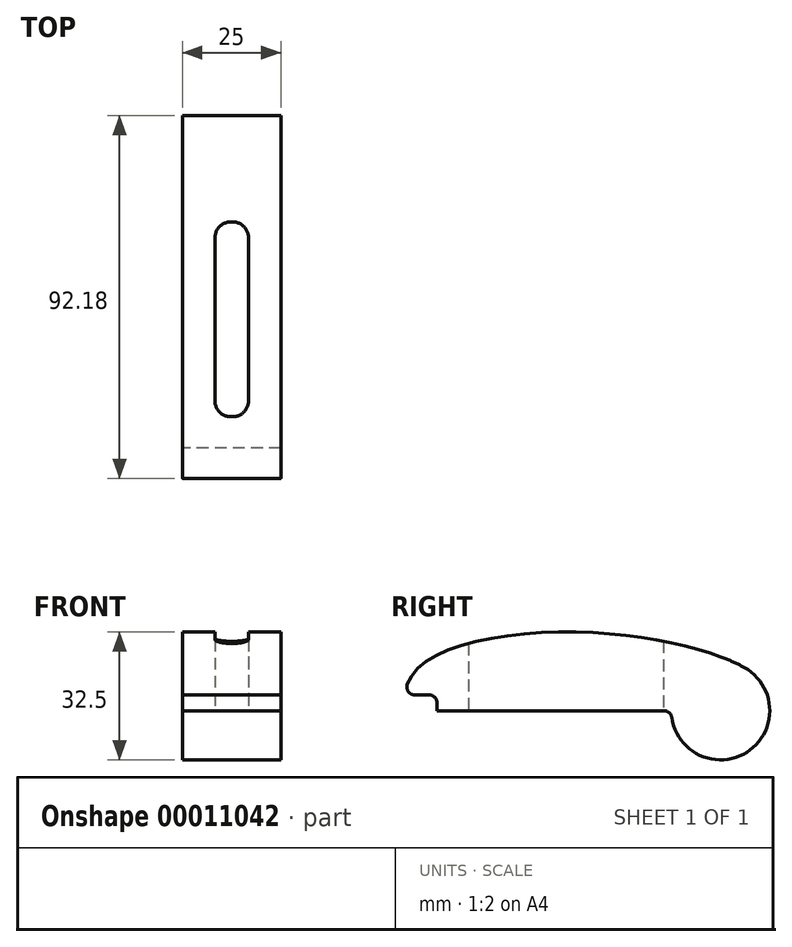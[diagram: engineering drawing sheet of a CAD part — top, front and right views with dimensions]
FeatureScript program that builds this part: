
annotation { "Feature Type Name" : "Feature", "Feature Type Description" : "" }
export const myFeature = defineFeature(function(context is Context, id is Id, definition is map)
    precondition{}
    {
        {
            var Q0;
            Q0=qCreatedBy(makeId("Right.planeOp"),FACE);
            var sketch = newSketch(context, id + "F0", { "sketchPlane" : qUnion([Q0])});
            skCircle(sketch, "E0", {"center": v(80, 0) * mm, "radius": 12.5 * mm});
            skLineSegment(sketch, "E1.bottom", {"start": v(0, 0) * mm, "end": v(80, 0) * mm});
            skLineSegment(sketch, "E1.top", {"start": v(0, 15) * mm, "end": v(80, 15) * mm, "construction": true});
            skLineSegment(sketch, "E1.left", {"start": v(0, 0) * mm, "end": v(0, 15) * mm, "construction": true});
            skLineSegment(sketch, "E1.right", {"start": v(80, 0) * mm, "end": v(80, 15) * mm});
            skLineSegment(sketch, "E2.bottom", {"start": v(0, 0) * mm, "end": v(8, 0) * mm});
            skLineSegment(sketch, "E2.top", {"start": v(0, 4) * mm, "end": v(8, 4) * mm});
            skLineSegment(sketch, "E2.left", {"start": v(0, 0) * mm, "end": v(0, 4) * mm});
            skLineSegment(sketch, "E2.right", {"start": v(8, 0) * mm, "end": v(8, 4) * mm});
            skFitSpline(sketch, "E3", {"points": [v(0, 4) * mm, v(40, 20) * mm, v(86.9, 10.42) * mm], "startDerivative": vector(0, 67.79) * mm, "endDerivative": vector(40.4, -26.8) * mm});
            skSolve(sketch);
        }
        {
            var Q0;
            {var subQ1=sQuery(id+"F0.wireOp",EDGE,"E0");var subQ6=makeQuery(id+"F0.imprint","INTERSECT",VERTEX,{"derivedFrom":[subQ1,sQuery(id+"F0.wireOp",EDGE,"E3")]});Q0=makeQuery(id+"F0.imprint","IMPRINT",FACE,{"disambiguationData":[TD([[makeQuery(id+"F0.imprint","IMPRINT",EDGE,{"disambiguationData":[TD([[subQ6,-1.0]])],"derivedFrom":subQ1}),1.0]])]});}
            var Q1;
            {var subQ0=sQuery(id+"F0.wireOp",EDGE,"E3");var subQ3=sQuery(id+"F0.wireOp",EDGE,"E0");var subQ4=makeQuery(id+"F0.imprint","INTERSECT",VERTEX,{"derivedFrom":[subQ3,subQ0]});Q1=makeQuery(id+"F0.imprint","IMPRINT",FACE,{"disambiguationData":[TD([[makeQuery(id+"F0.imprint","IMPRINT",EDGE,{"disambiguationData":[TD([[subQ4,-1.0]])],"derivedFrom":subQ3}),-1.0]])]});}
            var Q2;
            {var subQ1=sQuery(id+"F0.wireOp",EDGE,"E0");var subQ3=sQuery(id+"F0.wireOp",EDGE,"E1.bottom");var subQ5=makeQuery(id+"F0.imprint","INTERSECT",VERTEX,{"derivedFrom":[subQ1,subQ3]});Q2=makeQuery(id+"F0.imprint","IMPRINT",FACE,{"disambiguationData":[TD([[makeQuery(id+"F0.imprint","IMPRINT",EDGE,{"disambiguationData":[TD([[subQ5,1.0]])],"derivedFrom":subQ1}),1.0]])]});}
            var Q3;
            {var subQ3=sQuery(id+"F0.wireOp",EDGE,"E2.top");Q3=makeQuery(id+"F0.imprint","IMPRINT",FACE,{"disambiguationData":[TD([[makeQuery(id+"F0.imprint","IMPRINT",EDGE,{"derivedFrom":subQ3}),1.0]])]});}
            extrude(context, id + "F1", {"entities" : qUnion([Q0, Q1, Q2, Q3]), "depth" : 25 * mm});
        }
        {
            var Q0;
            Q0=qCreatedBy(makeId("Top.planeOp"),FACE);
            var sketch = newSketch(context, id + "F2", { "sketchPlane" : qUnion([Q0])});
            skLineSegment(sketch, "E4.bottom", {"start": v(12.25, 16) * mm, "end": v(12.75, 16) * mm});
            skLineSegment(sketch, "E4.top", {"start": v(12.25, 65.5) * mm, "end": v(12.75, 65.5) * mm});
            skLineSegment(sketch, "E4.left", {"start": v(8.25, 20) * mm, "end": v(8.25, 61.5) * mm});
            skLineSegment(sketch, "E4.right", {"start": v(16.75, 20) * mm, "end": v(16.75, 61.5) * mm});
            skLineSegment(sketch, "E5", {"start": v(0, 36.82) * mm, "end": v(8.25, 36.82) * mm, "construction": true});
            skLineSegment(sketch, "E6", {"start": v(16.75, 36.82) * mm, "end": v(25, 36.82) * mm, "construction": true});
            skPoint(sketch, "E7.visualSharp", {"position": v(8.25, 65.5) * mm});
            skArc(sketch, "E7.filletArc", {"start": v(12.25, 65.5) * mm, "mid": v(9.42, 64.33) * mm, "end": v(8.25, 61.5) * mm});
            skPoint(sketch, "E8.visualSharp", {"position": v(16.75, 65.5) * mm});
            skArc(sketch, "E8.filletArc", {"start": v(16.75, 61.5) * mm, "mid": v(15.58, 64.33) * mm, "end": v(12.75, 65.5) * mm});
            skPoint(sketch, "E9.visualSharp", {"position": v(16.75, 16) * mm});
            skArc(sketch, "E9.filletArc", {"start": v(12.75, 16) * mm, "mid": v(15.58, 17.17) * mm, "end": v(16.75, 20) * mm});
            skPoint(sketch, "E10.visualSharp", {"position": v(8.25, 16) * mm});
            skArc(sketch, "E10.filletArc", {"start": v(8.25, 20) * mm, "mid": v(9.42, 17.17) * mm, "end": v(12.25, 16) * mm});
            skSolve(sketch);
        }
        {
            var Q0;
            Q0 = qSketchRegion(id + "F2", true);
            extrude(context, id + "F3", {"entities" : qUnion([Q0]), "operationType" : NewBodyOperationType.REMOVE, "endBound" : BoundingType.THROUGH_ALL, "depth" : 25 * mm});
        }
        {
            var Q0;
            Q0=makeQuery(id+"F1.opExtrude","SWEPT_EDGE",EDGE,{"disambiguationData":[OSD([sQuery(id+"F0.wireOp",EDGE,"E0"),sQuery(id+"F0.wireOp",EDGE,"E1.bottom")])]});
            var Q1;
            Q1=makeQuery(id+"F1.opExtrude","SWEPT_EDGE",EDGE,{"disambiguationData":[OSD([sQuery(id+"F0.wireOp",EDGE,"E2.top"),sQuery(id+"F0.wireOp",EDGE,"E2.right")])]});
            var Q2;
            Q2=makeQuery(id+"F1.opExtrude","SWEPT_EDGE",EDGE,{"disambiguationData":[OSD([sQuery(id+"F0.wireOp",EDGE,"E2.top"),sQuery(id+"F0.wireOp",EDGE,"E2.left"),sQuery(id+"F0.wireOp",EDGE,"E3")])]});
            fillet(context, id + "F4", {"entities" : qUnion([Q0, Q1, Q2]), "radius" : 2 * mm, "tangentPropagation" : true, "allowEdgeOverflow" : false});
        }
    });
